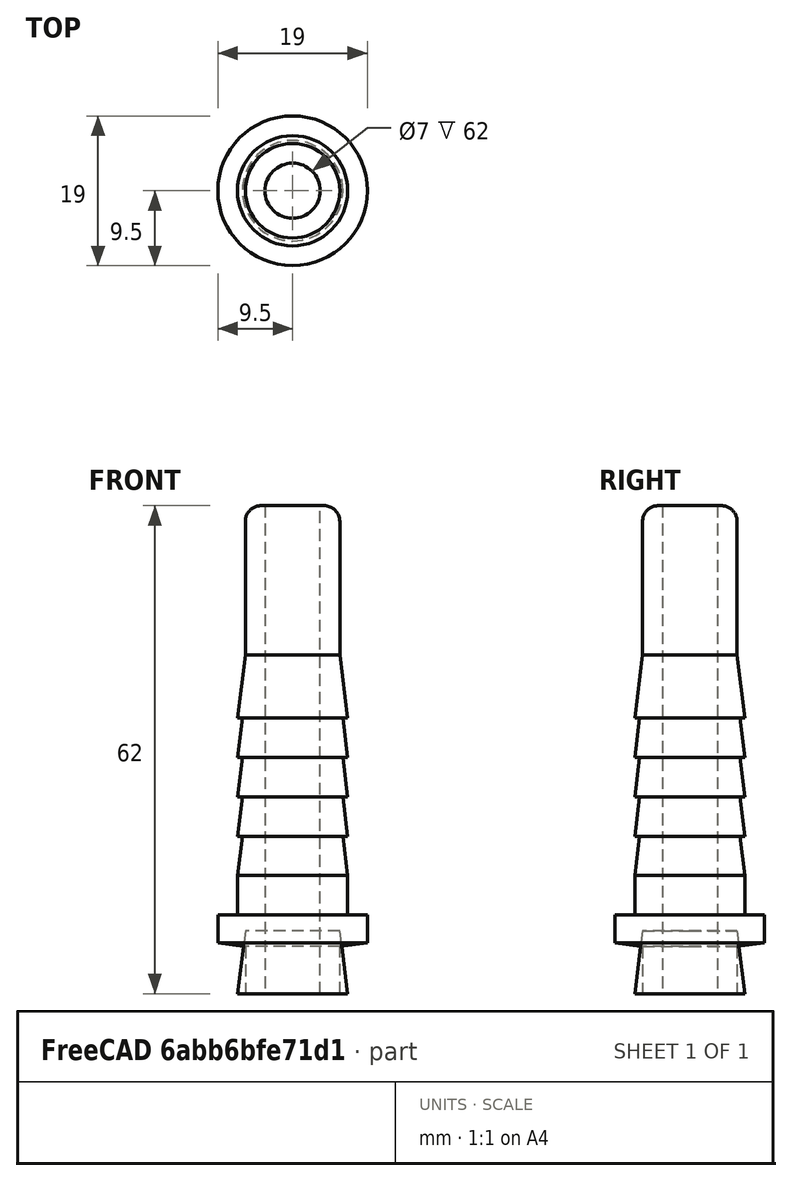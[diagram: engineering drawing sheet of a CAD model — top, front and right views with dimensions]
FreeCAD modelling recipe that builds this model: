
FCSTD DOCUMENT  (FreeCAD 1.1R1.1.0)
Label: HoseFitting_14423
License: All rights reserved
LicenseURL: http://en.wikipedia.org/wiki/All_rights_reserved
objects: Part::Cylinder×5, Part::MultiFuse×5, Part::Cone×2, Spreadsheet::Sheet×1, Part::FeaturePython×1, Part::Torus×1, Part::Cut×1
note: 14 computed .brp shape members not serialized (recipe doc carries the construction recipe); baked Part::Feature solids carry a one-line shape summary decoded from their .brp

FEATURE [Spreadsheet::Sheet] Spreadsheet  label="ISO14423"
  DN = 6
  cells = A1='Schlauchstutzen; O1='FL, FV max. length; R1='Weld connection; T1='Type G; AE1='Form R; AJ1='Form RI; AM1='Form RA; AR1='Klemmbackenschale; A2='Nennweite (DN); B2='d1 (OD); C2='d2; D2='d3 (ID); E2='d4; F2='d5; G2='f1; H2='k; I2='l2; J2='l3; K2='Default Rips; L2='l4; M2='l5; N2='r1; O2='l6; P2='l7; Q2='d6; R2='l8; S2='s1; T2='d7; U2='d8; V2='d9; W2='d10; X2='d11; Y2='l9; Z2='l10; AA2='l11; AB2='l12; AC2='l13; AD2='s; AE2='d12; AF2='l14; AG2='l15; AH2='l16; AI2='s; AJ2='d13; AK2='l17; AL2='l18; AM2='d15; AN2='l19; AO2='l20; AP2='l21; AQ2='S; AR2='b1; AS2='b2; AT2='d16; AU2='Rips; AV2='e1; AW2='e2; AX2='e3; AY2='e4; AZ2='f2; BA2='f3; BB2='l22; BC2='l23; BD2='l24; BE2='l25; BF2='r1; BG2='r2; BH2='r3; BI2='r4; BJ2='r5; A3==hiddenref(.DN.String); B3(d1)==.B10; C3(d2)==.C10; D3(d3)==.D10; E3(d4)==.E10; F3(d5)==.F10; G3(f1)==.G10; H3(k)==.H10; I3(l2)==.I10; J3(l3)==.J10; K3(rips)==.K10; L3(l4)==.L10; M3(l5)==.M10; N3(r1)==.N10; O3(l6)=; P3(l7)=; Q3(d6)=; R3(l8)=; S3(s1)=; T3(d7)=; U3(d8)=; V3(d9)=; W3(d10)=; X3(d11)=; Y3(l9)=; Z3(l10)=; AA3(l11)=; AB3(l12)=; AC3(l13)=; AD3(s_g)=; AE3(d12)=; AF3(l14)=; AG3(l15)=; AH3(l16)=; AI3(s_r)=; AJ3(d13)=; AK3(l17)=; AL3(l18)=; AM3(d15)=; AN3(l19)=; AO3(l20)=; AP3(l21)=; AQ3(s_ra)=; AR3(b1)=; AS3(b2)=; AT3(d16)=; AU3(rip_klemm)=; AV3(e1)=; AW3(e2)=; AX3(e3)=; AY3(e4)=; AZ3(f2)=; BA3(f3)=; BB3(l22)=; BC3(l23)=; BD3(l24)=; BE3(l25)=; BF3(r1_klemm)=; BG3(r2_klemm)=; BH3(r3_klemm)=; BI3(r4_klemm)=; BJ3(r5_klemm)=; A4='15; B4=13; C4=15; D4=9; E4=20; F4=13; G4=6; H4=4; I4=62; J4=9; K4=4; L4=8; M4=40; N4=2; O4=108; P4=108; Q4=21.3; R4=8; S4=3.2; T4==1 / 2; U4=18.3; V4=20; W4=13; X4=21.5; Y4=9.5; Z4=20.5; AA4=82.5; AB4=4; AC4=20; AD4=27; AE4=0.5; AF4=16; AG4=12; AH4=90; AI4=22; AJ4=24; AK4=17; AL4=79; AM4=28; AN4=12; AO4=9; AP4=83; AQ4=24; AR4=53; AS4=10.3; AT4=7; AU4=5; AV4=1.5; AW4=37; AX4=16; AY4=24.5; AZ4=8; BA4=3; BB4=65; BC4=4; BD4=14.5; BE4=3; BF4=12.5; BG4=6.75; BH4=9.5; BI4=10; BJ4=10.5; A5='20; B5=19; C5=21; D5=14; E5=26; F5=19; +379 more cells
  expr: .DN.Enum = cells[<<A4:|>>]
  expr: .cells.Bind.B3.BJ3 = tuple(.cells; <<B>> + str(hiddenref(DN) + 4); <<BJ>> + str(hiddenref(DN) + 4))
FEATURE [Part::Cylinder] Cylinder
  Angle = 360
  AttacherType = Attacher::AttachEngine3D
  FirstAngle = 0
  Height = 60
  Radius = 6
  SecondAngle = 0
  expr: Height = <<ISO14423>>.l2 - <<ISO14423>>.r1
  expr: Radius = <<ISO14423>>.d1 / 2
FEATURE [Part::Cone] Cone
  Angle = 360
  AttacherType = Attacher::AttachEngine3D
  Height = 8
  Radius1 = 7
  Radius2 = 6
  expr: Height = <<ISO14423>>.l4
  expr: Radius1 = <<ISO14423>>.d2 / 2
  expr: Radius2 = <<ISO14423>>.d1 / 2
FEATURE [Part::FeaturePython] Array  # Draft array (typed FeaturePython)
  AlwaysSyncPlacement = false
  Angle = 360
  ArrayType = 0
  Axis = (0,0,1)
  Base = -> Cone
  Center = (0,0,0)
  Count = 5
  ExpandArray = false
  Fuse = false
  IntervalAxis = (0,0,0)
  IntervalX = (100,0,0)
  IntervalY = (0,100,0)
  IntervalZ = (0,0,5)
  NumberCircles = 3
  NumberPolar = 5
  NumberX = 1
  NumberY = 1
  NumberZ = 5
  Placement = pos=(0,0,15) rot=(0,0,1;0rad)
  PlacementList = 5 placements: arithmetic series from (0,0,0) step (0,0,5) to (0,0,20)
  RadialDistance = 50
  ScaleList = (5) [(1,1,1),(1,1,1),(1,1,1),(1,1,1),(1,1,1)]
  Symmetry = 1
  TangentialDistance = 25
  expr: .IntervalZ.z = <<ISO14423>>.rips + 1
  expr: .Placement.Base.z = <<ISO14423>>.f1 + <<ISO14423>>.l3
  expr: NumberZ = <<ISO14423>>.rips + 1
FEATURE [Part::Cylinder] Cylinder001
  Angle = 360
  AttacherType = Attacher::AttachEngine3D
  FirstAngle = 0
  Height = 5
  Placement = pos=(0,0,10) rot=(0,0,1;0rad)
  Radius = 7
  SecondAngle = 0
  expr: .Placement.Base.z = <<ISO14423>>.f1 + <<ISO14423>>.k
  expr: Height = <<ISO14423>>.l3 - <<ISO14423>>.k
  expr: Radius = <<ISO14423>>.d2 / 2
FEATURE [Part::Cylinder] Cylinder002
  Angle = 360
  AttacherType = Attacher::AttachEngine3D
  FirstAngle = 0
  Height = 3.55918
  Placement = pos=(0,0,6.44082) rot=(0,0,1;0rad)
  Radius = 9.5
  SecondAngle = 0
  expr: .Placement.Base.z = <<ISO14423>>.f1 + tan(10) * (<<ISO14423>>.d4 - <<ISO14423>>.d2) / 2
  expr: Height = <<ISO14423>>.k - tan(10) * (<<ISO14423>>.d4 - <<ISO14423>>.d2) / 2
  expr: Radius = <<ISO14423>>.d4 / 2
FEATURE [Part::Cone] Cone001
  Angle = 360
  AttacherType = Attacher::AttachEngine3D
  Height = 0.440817
  Placement = pos=(0,0,6) rot=(0,0,1;0rad)
  Radius1 = 6
  Radius2 = 9.5
  expr: .Placement.Base.z = <<ISO14423>>.f1
  expr: Height = tan(10) * (<<ISO14423>>.d4 - <<ISO14423>>.d2) / 2
  expr: Radius1 = <<ISO14423>>.d5 / 2
  expr: Radius2 = <<ISO14423>>.d4 / 2
FEATURE [Part::Cylinder] Cylinder003
  Angle = 360
  AttacherType = Attacher::AttachEngine3D
  FirstAngle = 0
  Height = 62
  Radius = 3.5
  SecondAngle = 0
  expr: Height = <<ISO14423>>.l2
  expr: Radius = <<ISO14423>>.d3 / 2
FEATURE [Part::MultiFuse] Fusion
  Shapes = -> [Cone001,Cylinder001,Cylinder002]
FEATURE [Part::MultiFuse] Fusion002
  Shapes = -> [Array]
FEATURE [Part::Torus] Torus
  Angle1 = -180
  Angle2 = 180
  Angle3 = 360
  AttacherType = Attacher::AttachEngine3D
  Placement = pos=(0,0,60) rot=(0,0,1;0rad)
  Radius1 = 4
  Radius2 = 2
  expr: .Placement.Base.z = <<ISO14423>>.l2 - <<ISO14423>>.r1
  expr: Radius1 = <<ISO14423>>.d1 / 2 - <<ISO14423>>.r1
  expr: Radius2 = <<ISO14423>>.r1
FEATURE [Part::Cylinder] Cylinder004
  Angle = 360
  AttacherType = Attacher::AttachEngine3D
  FirstAngle = 0
  Height = 62
  Radius = 4
  SecondAngle = 0
  expr: Height = <<ISO14423>>.l2
  expr: Radius = <<ISO14423>>.d1 / 2 - <<ISO14423>>.r1
FEATURE [Part::MultiFuse] Fusion001
  Shapes = -> [Cylinder,Fusion,Cylinder004]
FEATURE [Part::MultiFuse] Fusion003
  Shapes = -> [Fusion001,Fusion002]
FEATURE [Part::MultiFuse] Fusion004
  Shapes = -> [Torus,Fusion003]
FEATURE [Part::Cut] Cut  label="Schlauchstutzen"
  Base = -> Fusion004
  Tool = -> Cylinder003
